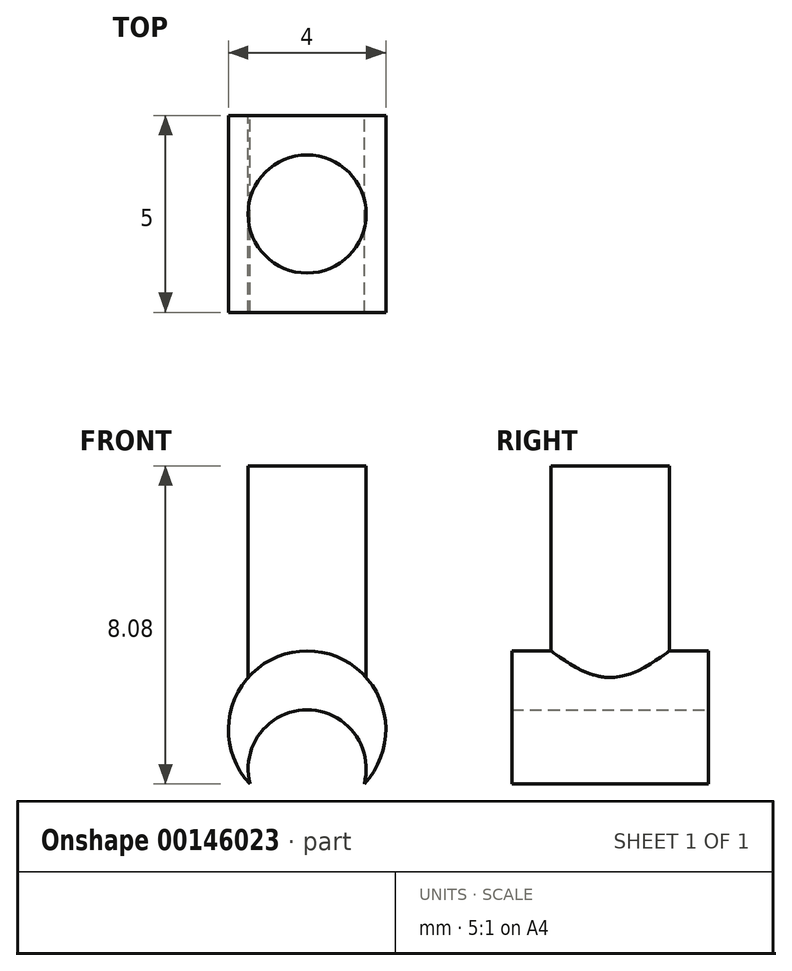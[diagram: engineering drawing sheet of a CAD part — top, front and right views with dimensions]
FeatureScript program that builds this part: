
annotation { "Feature Type Name" : "Feature", "Feature Type Description" : "" }
export const myFeature = defineFeature(function(context is Context, id is Id, definition is map)
    precondition{}
    {
        {
            var Q0;
            Q0=qCreatedBy(makeId("Front.planeOp"),FACE);
            var sketch = newSketch(context, id + "F0", { "sketchPlane" : qUnion([Q0])});
            skArc(sketch, "E0", {"start": v(1.45, -2.58) * mm, "mid": v(0, 0.8) * mm, "end": v(-1.45, -2.58) * mm});
            skArc(sketch, "E1", {"start": v(1.45, -2.58) * mm, "mid": v(0, -0.7) * mm, "end": v(-1.45, -2.58) * mm});
            skSolve(sketch);
        }
        {
            var Q0;
            Q0=qSketchRegion(id+"F0",true);
            extrude(context, id + "F1", {"entities" : qUnion([Q0]), "endBound" : BoundingType.SYMMETRIC, "depth" : 5 * mm});
        }
        {
            var Q0;
            Q0=qCreatedBy(makeId("Top.planeOp"),FACE);
            var sketch = newSketch(context, id + "F2", { "sketchPlane" : qUnion([Q0])});
            skCircle(sketch, "E2", {"center": v(0, 0) * mm, "radius": 1.5 * mm});
            skSolve(sketch);
        }
        {
            var Q0;
            Q0=qSketchRegion(id+"F2",true);
            extrude(context, id + "F3", {"entities" : qUnion([Q0]), "operationType" : NewBodyOperationType.ADD, "depth" : 5.5 * mm});
        }
    });
